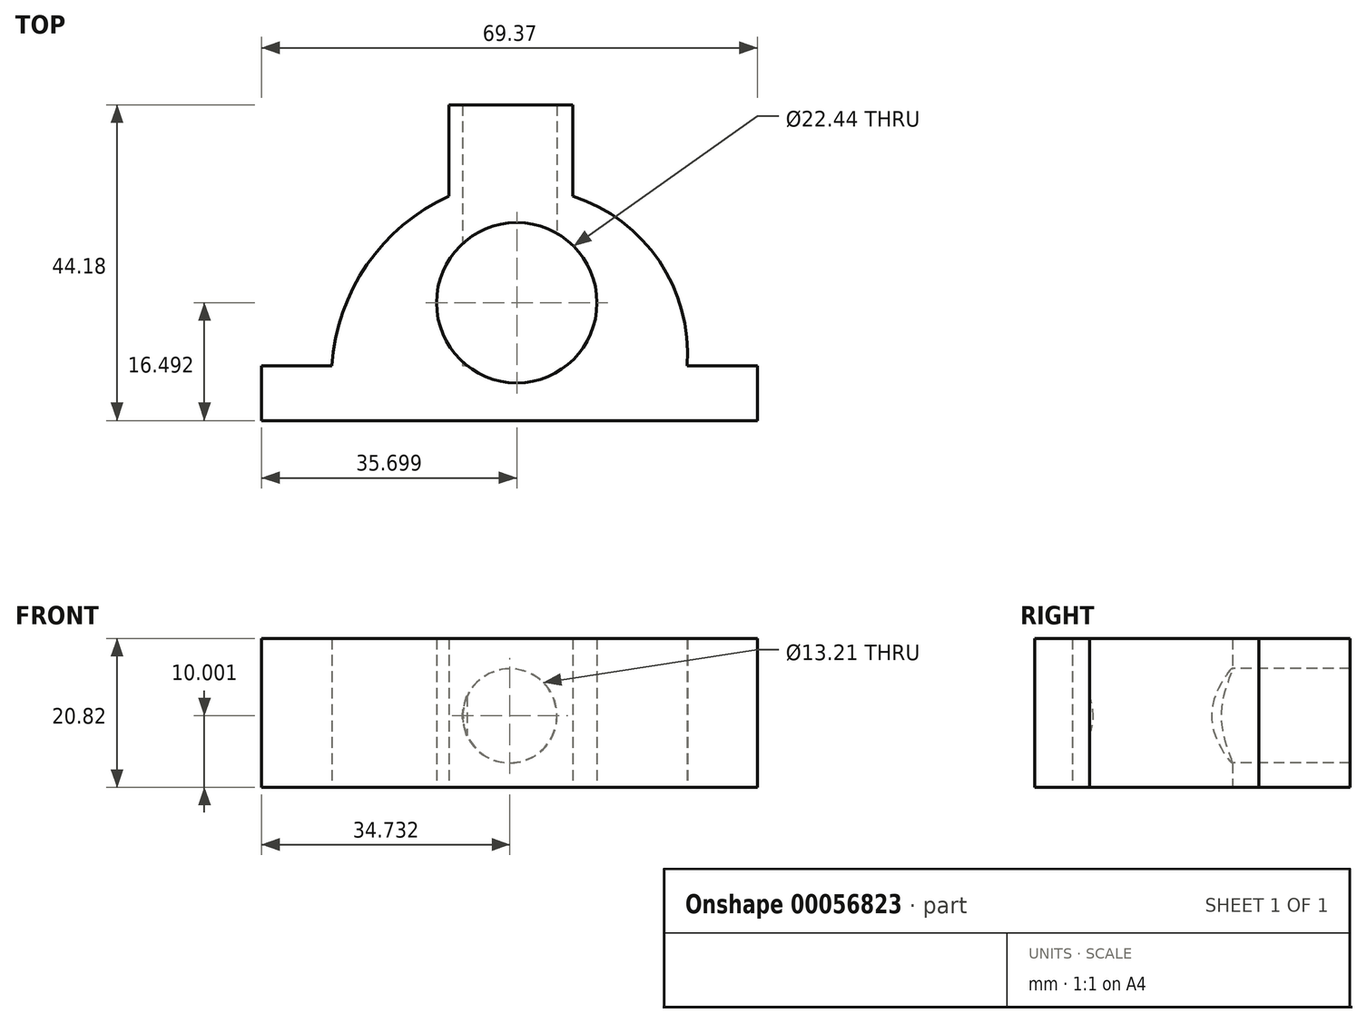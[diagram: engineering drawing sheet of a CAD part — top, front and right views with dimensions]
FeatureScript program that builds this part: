
annotation { "Feature Type Name" : "Feature", "Feature Type Description" : "" }
export const myFeature = defineFeature(function(context is Context, id is Id, definition is map)
    precondition{}
    {
        {
            var Q0;
            Q0=qCreatedBy(makeId("Top.planeOp"),FACE);
            var sketch = newSketch(context, id + "F0", { "sketchPlane" : qUnion([Q0])});
            skArc(sketch, "E0", {"start": v(-9.82, 0) * mm, "mid": v(-13.73, 14.63) * mm, "end": v(-25.85, 23.72) * mm});
            skArc(sketch, "E1", {"start": v(-43.2, 23.72) * mm, "mid": v(-54.64, 14.11) * mm, "end": v(-59.56, 0) * mm});
            skLineSegment(sketch, "E2", {"start": v(-9.82, 0) * mm, "end": v(0, 0) * mm});
            skLineSegment(sketch, "E3", {"start": v(0, 0) * mm, "end": v(0, -7.7) * mm});
            skLineSegment(sketch, "E4", {"start": v(-59.56, 0) * mm, "end": v(-69.37, 0) * mm});
            skLineSegment(sketch, "E5", {"start": v(-69.37, 0) * mm, "end": v(-69.37, -7.7) * mm});
            skLineSegment(sketch, "E6", {"start": v(-69.37, -7.7) * mm, "end": v(0, -7.7) * mm});
            skLineSegment(sketch, "E7", {"start": v(-43.2, 23.72) * mm, "end": v(-43.2, 36.49) * mm});
            skLineSegment(sketch, "E8", {"start": v(-43.2, 36.49) * mm, "end": v(-25.85, 36.49) * mm});
            skLineSegment(sketch, "E9", {"start": v(-25.85, 36.49) * mm, "end": v(-25.85, 23.72) * mm});
            skSolve(sketch);
        }
        {
            var Q0;
            Q0 = qSketchRegion(id + "F0", true);
            extrude(context, id + "F1", {"entities" : qUnion([Q0]), "depth" : 20.82 * mm});
        }
        {
            var Q0;
            Q0=qCreatedBy(makeId("Top.planeOp"),FACE);
            var sketch = newSketch(context, id + "F2", { "sketchPlane" : qUnion([Q0])});
            skCircle(sketch, "E10", {"center": v(-33.67, 8.8) * mm, "radius": 11.22 * mm});
            skSolve(sketch);
        }
        {
            var Q0;
            Q0 = qSketchRegion(id + "F2", true);
            extrude(context, id + "F3", {"entities" : qUnion([Q0]), "operationType" : NewBodyOperationType.REMOVE, "depth" : 25.4 * mm});
        }
        {
            var Q0;
            Q0=qCreatedBy(makeId("Front.planeOp"),FACE);
            var sketch = newSketch(context, id + "F4", { "sketchPlane" : qUnion([Q0])});
            skCircle(sketch, "E11", {"center": v(-34.64, 10) * mm, "radius": 6.6 * mm});
            skSolve(sketch);
        }
        {
            var Q0;
            Q0 = qSketchRegion(id + "F4", true);
            extrude(context, id + "F5", {"entities" : qUnion([Q0]), "operationType" : NewBodyOperationType.REMOVE, "oppositeDirection" : true, "depth" : 39.33 * mm});
        }
    });
